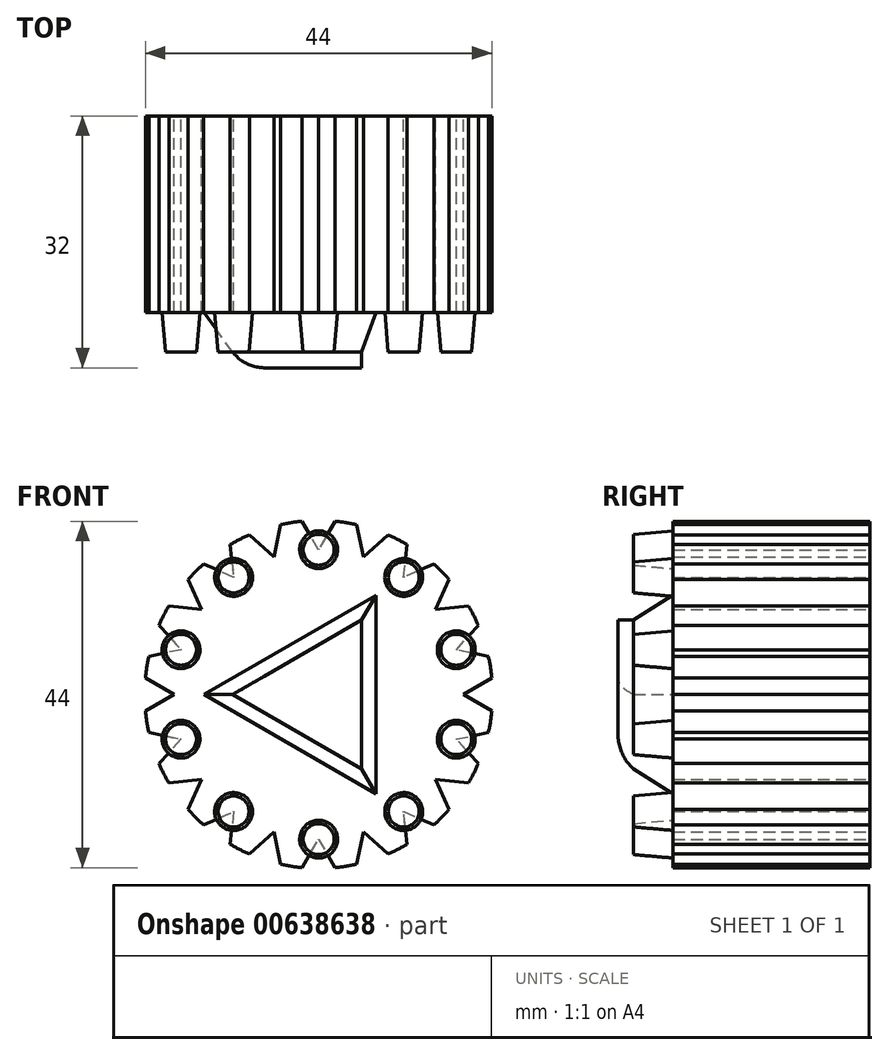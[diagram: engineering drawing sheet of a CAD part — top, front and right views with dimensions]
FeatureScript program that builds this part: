
annotation { "Feature Type Name" : "Feature", "Feature Type Description" : "" }
export const myFeature = defineFeature(function(context is Context, id is Id, definition is map)
    precondition{}
    {
        {
            var Q0;
            Q0=qCreatedBy(makeId("Front.planeOp"),FACE);
            var sketch = newSketch(context, id + "F0", { "sketchPlane" : qUnion([Q0])});
            skCircle(sketch, "E0", {"center": v(0, 0) * mm, "radius": 22.1 * mm});
            skLineSegment(sketch, "E1", {"start": v(-6.86, 30.26) * mm, "end": v(6.86, 30.26) * mm});
            skLineSegment(sketch, "E2", {"start": v(6.86, 30.26) * mm, "end": v(0, 18.38) * mm});
            skLineSegment(sketch, "E3", {"start": v(0, 18.38) * mm, "end": v(-6.86, 30.26) * mm});
            skLineSegment(sketch, "E4.1.0", {"start": v(-15.87, 26.66) * mm, "end": v(-2.83, 30.9) * mm});
            skLineSegment(sketch, "E4.1.1", {"start": v(-5.68, 17.48) * mm, "end": v(-15.87, 26.66) * mm});
            skLineSegment(sketch, "E4.1.2", {"start": v(-2.83, 30.9) * mm, "end": v(-5.68, 17.48) * mm});
            skLineSegment(sketch, "E4.2.0", {"start": v(-23.33, 20.45) * mm, "end": v(-12.24, 28.51) * mm});
            skLineSegment(sketch, "E4.2.1", {"start": v(-10.8, 14.87) * mm, "end": v(-23.33, 20.45) * mm});
            skLineSegment(sketch, "E4.2.2", {"start": v(-12.24, 28.51) * mm, "end": v(-10.8, 14.87) * mm});
            skLineSegment(sketch, "E4.3.0", {"start": v(-28.51, 12.24) * mm, "end": v(-20.45, 23.33) * mm});
            skLineSegment(sketch, "E4.3.1", {"start": v(-14.87, 10.8) * mm, "end": v(-28.51, 12.24) * mm});
            skLineSegment(sketch, "E4.3.2", {"start": v(-20.45, 23.33) * mm, "end": v(-14.87, 10.8) * mm});
            skLineSegment(sketch, "E4.4.0", {"start": v(-30.9, 2.83) * mm, "end": v(-26.66, 15.87) * mm});
            skLineSegment(sketch, "E4.4.1", {"start": v(-17.48, 5.68) * mm, "end": v(-30.9, 2.83) * mm});
            skLineSegment(sketch, "E4.4.2", {"start": v(-26.66, 15.87) * mm, "end": v(-17.48, 5.68) * mm});
            skLineSegment(sketch, "E4.5.0", {"start": v(-30.26, -6.86) * mm, "end": v(-30.26, 6.86) * mm});
            skLineSegment(sketch, "E4.5.1", {"start": v(-18.38, 0) * mm, "end": v(-30.26, -6.86) * mm});
            skLineSegment(sketch, "E4.5.2", {"start": v(-30.26, 6.86) * mm, "end": v(-18.38, 0) * mm});
            skLineSegment(sketch, "E4.6.0", {"start": v(-26.66, -15.87) * mm, "end": v(-30.9, -2.83) * mm});
            skLineSegment(sketch, "E4.6.1", {"start": v(-17.48, -5.68) * mm, "end": v(-26.66, -15.87) * mm});
            skLineSegment(sketch, "E4.6.2", {"start": v(-30.9, -2.83) * mm, "end": v(-17.48, -5.68) * mm});
            skLineSegment(sketch, "E4.7.0", {"start": v(-20.45, -23.33) * mm, "end": v(-28.51, -12.24) * mm});
            skLineSegment(sketch, "E4.7.1", {"start": v(-14.87, -10.8) * mm, "end": v(-20.45, -23.33) * mm});
            skLineSegment(sketch, "E4.7.2", {"start": v(-28.51, -12.24) * mm, "end": v(-14.87, -10.8) * mm});
            skLineSegment(sketch, "E4.8.0", {"start": v(-12.24, -28.51) * mm, "end": v(-23.33, -20.45) * mm});
            skLineSegment(sketch, "E4.8.1", {"start": v(-10.8, -14.87) * mm, "end": v(-12.24, -28.51) * mm});
            skLineSegment(sketch, "E4.8.2", {"start": v(-23.33, -20.45) * mm, "end": v(-10.8, -14.87) * mm});
            skLineSegment(sketch, "E4.9.0", {"start": v(-2.83, -30.9) * mm, "end": v(-15.87, -26.66) * mm});
            skLineSegment(sketch, "E4.9.1", {"start": v(-5.68, -17.48) * mm, "end": v(-2.83, -30.9) * mm});
            skLineSegment(sketch, "E4.9.2", {"start": v(-15.87, -26.66) * mm, "end": v(-5.68, -17.48) * mm});
            skLineSegment(sketch, "E4.10.0", {"start": v(6.86, -30.26) * mm, "end": v(-6.86, -30.26) * mm});
            skLineSegment(sketch, "E4.10.1", {"start": v(0, -18.38) * mm, "end": v(6.86, -30.26) * mm});
            skLineSegment(sketch, "E4.10.2", {"start": v(-6.86, -30.26) * mm, "end": v(0, -18.38) * mm});
            skLineSegment(sketch, "E4.11.0", {"start": v(15.87, -26.66) * mm, "end": v(2.83, -30.9) * mm});
            skLineSegment(sketch, "E4.11.1", {"start": v(5.68, -17.48) * mm, "end": v(15.87, -26.66) * mm});
            skLineSegment(sketch, "E4.11.2", {"start": v(2.83, -30.9) * mm, "end": v(5.68, -17.48) * mm});
            skLineSegment(sketch, "E4.12.0", {"start": v(23.33, -20.45) * mm, "end": v(12.24, -28.51) * mm});
            skLineSegment(sketch, "E4.12.1", {"start": v(10.8, -14.87) * mm, "end": v(23.33, -20.45) * mm});
            skLineSegment(sketch, "E4.12.2", {"start": v(12.24, -28.51) * mm, "end": v(10.8, -14.87) * mm});
            skLineSegment(sketch, "E4.13.0", {"start": v(28.51, -12.24) * mm, "end": v(20.45, -23.33) * mm});
            skLineSegment(sketch, "E4.13.1", {"start": v(14.87, -10.8) * mm, "end": v(28.51, -12.24) * mm});
            skLineSegment(sketch, "E4.13.2", {"start": v(20.45, -23.33) * mm, "end": v(14.87, -10.8) * mm});
            skLineSegment(sketch, "E4.14.0", {"start": v(30.9, -2.83) * mm, "end": v(26.66, -15.87) * mm});
            skLineSegment(sketch, "E4.14.1", {"start": v(17.48, -5.68) * mm, "end": v(30.9, -2.83) * mm});
            skLineSegment(sketch, "E4.14.2", {"start": v(26.66, -15.87) * mm, "end": v(17.48, -5.68) * mm});
            skLineSegment(sketch, "E4.15.0", {"start": v(30.26, 6.86) * mm, "end": v(30.26, -6.86) * mm});
            skLineSegment(sketch, "E4.15.1", {"start": v(18.38, 0) * mm, "end": v(30.26, 6.86) * mm});
            skLineSegment(sketch, "E4.15.2", {"start": v(30.26, -6.86) * mm, "end": v(18.38, 0) * mm});
            skLineSegment(sketch, "E4.16.0", {"start": v(26.66, 15.87) * mm, "end": v(30.9, 2.83) * mm});
            skLineSegment(sketch, "E4.16.1", {"start": v(17.48, 5.68) * mm, "end": v(26.66, 15.87) * mm});
            skLineSegment(sketch, "E4.16.2", {"start": v(30.9, 2.83) * mm, "end": v(17.48, 5.68) * mm});
            skLineSegment(sketch, "E4.17.0", {"start": v(20.45, 23.33) * mm, "end": v(28.51, 12.24) * mm});
            skLineSegment(sketch, "E4.17.1", {"start": v(14.87, 10.8) * mm, "end": v(20.45, 23.33) * mm});
            skLineSegment(sketch, "E4.17.2", {"start": v(28.51, 12.24) * mm, "end": v(14.87, 10.8) * mm});
            skLineSegment(sketch, "E4.18.0", {"start": v(12.24, 28.51) * mm, "end": v(23.33, 20.45) * mm});
            skLineSegment(sketch, "E4.18.1", {"start": v(10.8, 14.87) * mm, "end": v(12.24, 28.51) * mm});
            skLineSegment(sketch, "E4.18.2", {"start": v(23.33, 20.45) * mm, "end": v(10.8, 14.87) * mm});
            skLineSegment(sketch, "E4.19.0", {"start": v(2.83, 30.9) * mm, "end": v(15.87, 26.66) * mm});
            skLineSegment(sketch, "E4.19.1", {"start": v(5.68, 17.48) * mm, "end": v(2.83, 30.9) * mm});
            skLineSegment(sketch, "E4.19.2", {"start": v(15.87, 26.66) * mm, "end": v(5.68, 17.48) * mm});
            skSolve(sketch);
        }
        {
            var Q0;
            {var subQ3=sQuery(id+"F0.wireOp",EDGE,"E0");var subQ37=sQuery(id+"F0.wireOp",EDGE,"E4.16.2");var subQ62=makeQuery(id+"F0.imprint","INTERSECT",VERTEX,{"derivedFrom":[subQ3,subQ37]});Q0=makeQuery(id+"F0.imprint","IMPRINT",FACE,{"disambiguationData":[TD([[makeQuery(id+"F0.imprint","IMPRINT",EDGE,{"disambiguationData":[TD([[subQ62,1.0]])],"derivedFrom":subQ3}),1.0]])]});}
            extrude(context, id + "F1", {"entities" : qUnion([Q0]), "depth" : 25 * mm, "offsetDistance" : 25 * mm});
        }
        {
            var Q0;
            Q0=makeQuery(id+"F1.opExtrude","CAP_FACE",FACE,{"disambiguationData":[OSD([sQuery(id+"F0.wireOp",EDGE,"E0"),sQuery(id+"F0.wireOp",EDGE,"E2"),sQuery(id+"F0.wireOp",EDGE,"E3"),sQuery(id+"F0.wireOp",EDGE,"E4.1.1"),sQuery(id+"F0.wireOp",EDGE,"E4.1.2"),sQuery(id+"F0.wireOp",EDGE,"E4.2.1"),sQuery(id+"F0.wireOp",EDGE,"E4.2.2"),sQuery(id+"F0.wireOp",EDGE,"E4.3.1"),sQuery(id+"F0.wireOp",EDGE,"E4.3.2"),sQuery(id+"F0.wireOp",EDGE,"E4.4.1"),sQuery(id+"F0.wireOp",EDGE,"E4.4.2"),sQuery(id+"F0.wireOp",EDGE,"E4.5.1"),sQuery(id+"F0.wireOp",EDGE,"E4.5.2"),sQuery(id+"F0.wireOp",EDGE,"E4.6.1"),sQuery(id+"F0.wireOp",EDGE,"E4.6.2"),sQuery(id+"F0.wireOp",EDGE,"E4.7.1"),sQuery(id+"F0.wireOp",EDGE,"E4.7.2"),sQuery(id+"F0.wireOp",EDGE,"E4.8.1"),sQuery(id+"F0.wireOp",EDGE,"E4.8.2"),sQuery(id+"F0.wireOp",EDGE,"E4.9.1"),sQuery(id+"F0.wireOp",EDGE,"E4.9.2"),sQuery(id+"F0.wireOp",EDGE,"E4.10.1"),sQuery(id+"F0.wireOp",EDGE,"E4.10.2"),sQuery(id+"F0.wireOp",EDGE,"E4.11.1"),sQuery(id+"F0.wireOp",EDGE,"E4.11.2"),sQuery(id+"F0.wireOp",EDGE,"E4.12.1"),sQuery(id+"F0.wireOp",EDGE,"E4.12.2"),sQuery(id+"F0.wireOp",EDGE,"E4.13.1"),sQuery(id+"F0.wireOp",EDGE,"E4.13.2"),sQuery(id+"F0.wireOp",EDGE,"E4.14.1"),sQuery(id+"F0.wireOp",EDGE,"E4.14.2"),sQuery(id+"F0.wireOp",EDGE,"E4.15.1"),sQuery(id+"F0.wireOp",EDGE,"E4.15.2"),sQuery(id+"F0.wireOp",EDGE,"E4.16.1"),sQuery(id+"F0.wireOp",EDGE,"E4.16.2"),sQuery(id+"F0.wireOp",EDGE,"E4.17.1"),sQuery(id+"F0.wireOp",EDGE,"E4.17.2"),sQuery(id+"F0.wireOp",EDGE,"E4.18.1"),sQuery(id+"F0.wireOp",EDGE,"E4.18.2"),sQuery(id+"F0.wireOp",EDGE,"E4.19.1"),sQuery(id+"F0.wireOp",EDGE,"E4.19.2")])],"isStart":false});
            var sketch = newSketch(context, id + "F2", { "sketchPlane" : qUnion([Q0])});
            skCircle(sketch, "E5", {"center": v(0, 18.38) * mm, "radius": 2.4 * mm});
            skCircle(sketch, "E6.1.0", {"center": v(-10.8, 14.87) * mm, "radius": 2.4 * mm});
            skCircle(sketch, "E6.2.0", {"center": v(-17.48, 5.68) * mm, "radius": 2.4 * mm});
            skCircle(sketch, "E6.3.0", {"center": v(-17.48, -5.68) * mm, "radius": 2.4 * mm});
            skCircle(sketch, "E6.4.0", {"center": v(-10.8, -14.87) * mm, "radius": 2.4 * mm});
            skCircle(sketch, "E6.5.0", {"center": v(0, -18.38) * mm, "radius": 2.4 * mm});
            skCircle(sketch, "E6.6.0", {"center": v(10.8, -14.87) * mm, "radius": 2.4 * mm});
            skCircle(sketch, "E6.7.0", {"center": v(17.48, -5.68) * mm, "radius": 2.4 * mm});
            skCircle(sketch, "E6.8.0", {"center": v(17.48, 5.68) * mm, "radius": 2.4 * mm});
            skCircle(sketch, "E6.9.0", {"center": v(10.8, 14.87) * mm, "radius": 2.4 * mm});
            skPoint(sketch, "E6.center", {"position": v(0, 0) * mm});
            skSolve(sketch);
        }
        {
            var Q0;
            Q0 = qSketchRegion(id + "F2", true);
            extrude(context, id + "F3", {"entities" : qUnion([Q0]), "operationType" : NewBodyOperationType.ADD, "depth" : 5 * mm, "offsetDistance" : 25 * mm, "hasDraft" : true, "draftAngle" : 5 * degree, "draftPullDirection" : true});
        }
        {
            var Q0;
            Q0=makeQuery(id+"F1.opExtrude","CAP_FACE",FACE,{"disambiguationData":[OSD([sQuery(id+"F0.wireOp",EDGE,"E0"),sQuery(id+"F0.wireOp",EDGE,"E2"),sQuery(id+"F0.wireOp",EDGE,"E3"),sQuery(id+"F0.wireOp",EDGE,"E4.1.1"),sQuery(id+"F0.wireOp",EDGE,"E4.1.2"),sQuery(id+"F0.wireOp",EDGE,"E4.2.1"),sQuery(id+"F0.wireOp",EDGE,"E4.2.2"),sQuery(id+"F0.wireOp",EDGE,"E4.3.1"),sQuery(id+"F0.wireOp",EDGE,"E4.3.2"),sQuery(id+"F0.wireOp",EDGE,"E4.4.1"),sQuery(id+"F0.wireOp",EDGE,"E4.4.2"),sQuery(id+"F0.wireOp",EDGE,"E4.5.1"),sQuery(id+"F0.wireOp",EDGE,"E4.5.2"),sQuery(id+"F0.wireOp",EDGE,"E4.6.1"),sQuery(id+"F0.wireOp",EDGE,"E4.6.2"),sQuery(id+"F0.wireOp",EDGE,"E4.7.1"),sQuery(id+"F0.wireOp",EDGE,"E4.7.2"),sQuery(id+"F0.wireOp",EDGE,"E4.8.1"),sQuery(id+"F0.wireOp",EDGE,"E4.8.2"),sQuery(id+"F0.wireOp",EDGE,"E4.9.1"),sQuery(id+"F0.wireOp",EDGE,"E4.9.2"),sQuery(id+"F0.wireOp",EDGE,"E4.10.1"),sQuery(id+"F0.wireOp",EDGE,"E4.10.2"),sQuery(id+"F0.wireOp",EDGE,"E4.11.1"),sQuery(id+"F0.wireOp",EDGE,"E4.11.2"),sQuery(id+"F0.wireOp",EDGE,"E4.12.1"),sQuery(id+"F0.wireOp",EDGE,"E4.12.2"),sQuery(id+"F0.wireOp",EDGE,"E4.13.1"),sQuery(id+"F0.wireOp",EDGE,"E4.13.2"),sQuery(id+"F0.wireOp",EDGE,"E4.14.1"),sQuery(id+"F0.wireOp",EDGE,"E4.14.2"),sQuery(id+"F0.wireOp",EDGE,"E4.15.1"),sQuery(id+"F0.wireOp",EDGE,"E4.15.2"),sQuery(id+"F0.wireOp",EDGE,"E4.16.1"),sQuery(id+"F0.wireOp",EDGE,"E4.16.2"),sQuery(id+"F0.wireOp",EDGE,"E4.17.1"),sQuery(id+"F0.wireOp",EDGE,"E4.17.2"),sQuery(id+"F0.wireOp",EDGE,"E4.18.1"),sQuery(id+"F0.wireOp",EDGE,"E4.18.2"),sQuery(id+"F0.wireOp",EDGE,"E4.19.1"),sQuery(id+"F0.wireOp",EDGE,"E4.19.2")])],"isStart":false});
            var sketch = newSketch(context, id + "F4", { "sketchPlane" : qUnion([Q0])});
            skCircle(sketch, "E7.cCircle", {"center": v(0, 0) * mm, "radius": 7.28 * mm, "construction": true});
            skLineSegment(sketch, "E7.0", {"start": v(7.28, 12.6) * mm, "end": v(7.28, -12.6) * mm});
            skLineSegment(sketch, "E7.1", {"start": v(7.28, -12.6) * mm, "end": v(-14.55, 0) * mm});
            skLineSegment(sketch, "E7.2", {"start": v(-14.55, 0) * mm, "end": v(7.28, 12.6) * mm});
            skPoint(sketch, "E7.0.midPoint", {"position": v(7.28, 0) * mm});
            skSolve(sketch);
        }
        {
            var Q0;
            Q0=makeQuery(id+"F4.imprint","IMPRINT",FACE,{"disambiguationData":[TD([[makeQuery(id+"F4.imprint","IMPRINT",EDGE,{"derivedFrom":sQuery(id+"F4.wireOp",EDGE,"E7.0")}),-1.0]])]});
            var Q1;
            Q1=sQuery(id+"F4.wireOp",EDGE,"E7.2");
            var Q2;
            Q2=sQuery(id+"F4.wireOp",EDGE,"E7.0");
            var Q3;
            Q3=sQuery(id+"F4.wireOp",EDGE,"E7.1");
            extrude(context, id + "F5", {"entities" : qUnion([Q0]), "operationType" : NewBodyOperationType.ADD, "surfaceEntities" : qUnion([Q1, Q2, Q3]), "depth" : 5 * mm, "offsetDistance" : 25 * mm, "hasDraft" : true, "draftAngle" : 20 * degree, "draftPullDirection" : true});
        }
        {
            var Q0;
            Q0=makeQuery(id+"F5.opExtrude","CAP_FACE",FACE,{"disambiguationData":[OSD([sQuery(id+"F4.wireOp",EDGE,"E7.0"),sQuery(id+"F4.wireOp",EDGE,"E7.1"),sQuery(id+"F4.wireOp",EDGE,"E7.2")])],"isStart":false});
            extrude(context, id + "F6", {"entities" : qUnion([Q0]), "operationType" : NewBodyOperationType.ADD, "depth" : 2 * mm, "offsetDistance" : 25 * mm});
        }
        {
            var Q0;
            Q0=makeQuery(id+"F6.opExtrude","CAP_EDGE",EDGE,{"disambiguationData":[OSD([sQuery(id+"F4.wireOp",EDGE,"E7.1")])],"isStart":false});
            var Q1;
            Q1=makeQuery(id+"F5.opExtrude","CAP_EDGE",EDGE,{"disambiguationData":[OSD([sQuery(id+"F4.wireOp",EDGE,"E7.1")])],"isStart":true});
            fillet(context, id + "F7", {"entities" : qUnion([Q0, Q1]), "radius" : 5 * mm, "tangentPropagation" : true, "allowEdgeOverflow" : false});
        }
    });
